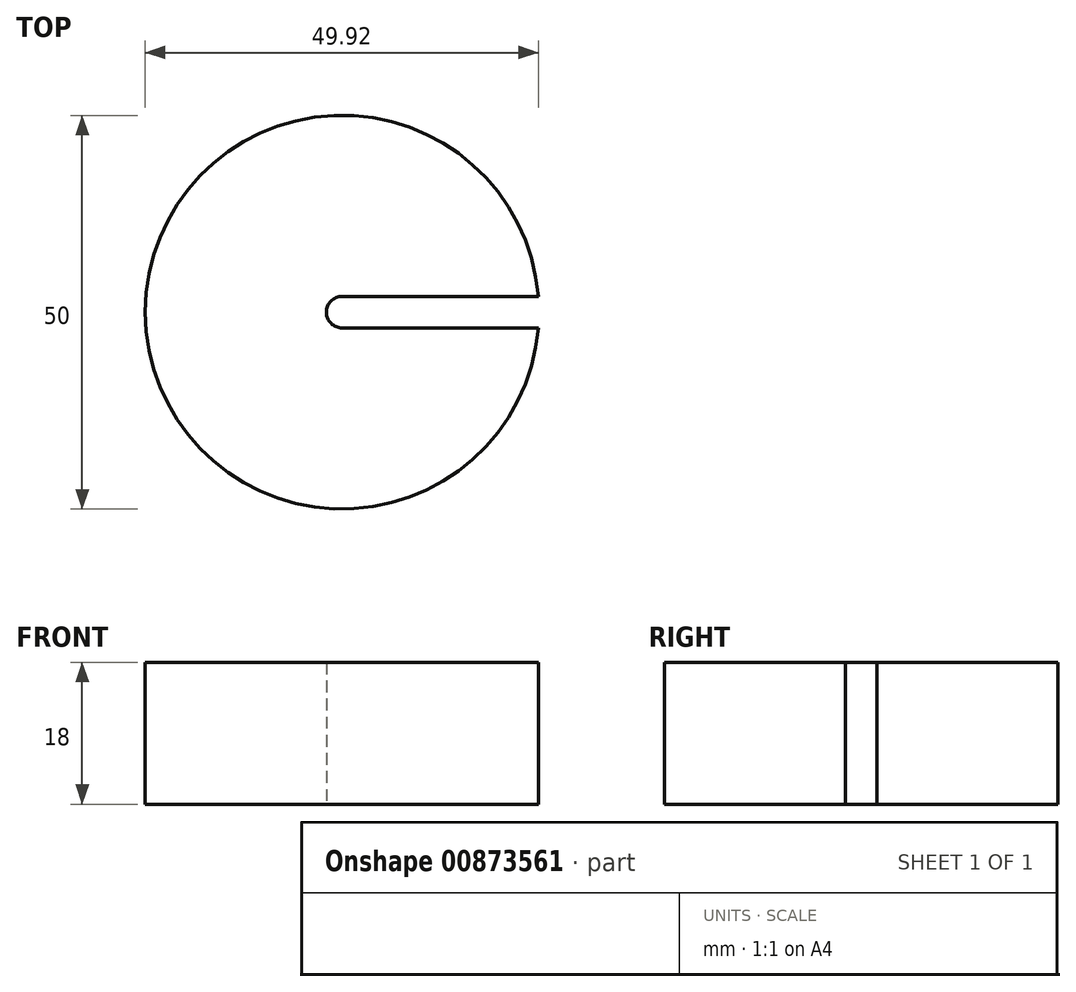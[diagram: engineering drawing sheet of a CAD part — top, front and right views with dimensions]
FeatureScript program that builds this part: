
annotation { "Feature Type Name" : "Feature", "Feature Type Description" : "" }
export const myFeature = defineFeature(function(context is Context, id is Id, definition is map)
    precondition{}
    {
        {
            var Q0;
            Q0=qCreatedBy(makeId("Top.planeOp"),FACE);
            var sketch = newSketch(context, id + "F0", { "sketchPlane" : qUnion([Q0])});
            skCircle(sketch, "E0", {"center": v(0, 0) * mm, "radius": 25 * mm});
            skCircle(sketch, "E1", {"center": v(0, 0) * mm, "radius": 2 * mm});
            skLineSegment(sketch, "E2", {"start": v(0, 2) * mm, "end": v(24.92, 2) * mm});
            skLineSegment(sketch, "E3", {"start": v(0, -2) * mm, "end": v(24.92, -2) * mm});
            skSolve(sketch);
        }
        {
            var Q0;
            {var subQ0=sQuery(id+"F0.wireOp",EDGE,"E2");Q0=makeQuery(id+"F0.imprint","IMPRINT",FACE,{"disambiguationData":[TD([[makeQuery(id+"F0.imprint","IMPRINT",EDGE,{"derivedFrom":subQ0}),1.0]])]});}
            extrude(context, id + "F1", {"entities" : qUnion([Q0]), "flatOperationType" : FlatOperationType.REMOVE, "depth" : 18 * mm, "offsetDistance" : 25 * mm, "domain" : OperationDomain.MODEL});
        }
    });
